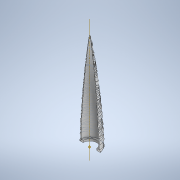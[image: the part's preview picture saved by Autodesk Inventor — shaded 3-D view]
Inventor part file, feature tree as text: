
AUTODESK INVENTOR PART (.ipt)
format: ipt  version: 2022 (Build 260153000, 153)  size: 3,374,080 bytes
history: native  units: in
note: dims shown in document units (in); Inventor stores cm internally (conversion verified against a paired STEP export)
features: sketch x9, helix x6, other x4, revolve x2, fillet x2, extrude x1
ambient origin geometry x8: Origin, YZ Plane, XZ Plane, XY Plane, X Axis, Y Axis, Z Axis, Center Point
bodies: Solid1 (feature_tree)
feature tree (24):
  other  "CrossSection1"
  other  "CrossSection2"
  extrude  "Extrusion1"  Depth=0.1969in
  revolve  "Revolution1"  Angle=360.0deg
  other  "Work Axis3"
  helix  "Coil3"  [1 undecoded]
  revolve  "Revolution2"  [1 undecoded]
  fillet  "Fillet2"  Radius=0.7677in
  other  "Work Axis7"
  helix  "Coil2"  [1 undecoded]
  fillet  "Fillet4"  Radius=0.1969in
  helix  "Coil4"  [1 undecoded]
  helix  "Coil5"  [1 undecoded]
  helix  "Coil6"  [1 undecoded]
  helix  "Coil7"  [1 undecoded]
  sketch  "Sketch1"  dims[d0=1.1811in d1=0.1969in]
  sketch  "Sketch2"  dims[d2=0.1181in d3=0.0in d7=360.0deg d8=0.4331in]
  sketch  "Sketch3"  dims[d19=0.4724in d20=0.2362in d21=0.7677in d22=360.0deg d24=0.1969in d26=0.1969in]
  sketch  "Sketch4"  dims[d29=1.5748in d30=0.3937in d31=1.378in d32=0.0447in d33=90.0deg d34=90.0deg d35=0.0in d36=0.0in d42=0.0787in d44=43.5197in d45=43.5039in]
  sketch  "Sketch5"  dims[d50=0.0in]
  sketch  "Sketch6"  dims[d54=0.3937in d55=0.3937in d56=5.5118in d57=-0.0275in d58=90.0deg d59=90.0deg d60=0.0in d61=0.0in]
  sketch  "Sketch7"  dims[d62=0.3937in]
  sketch  "Sketch8"  dims[d63=0.7677in]
  sketch  "Sketch9"  dims[d64=0.2362in d65=0.1575in d66=5.7087in d68=0.0394in d69=5.5118in d70=0.053in d71=0.0344in d72=0.0305in d73=0.1969in d74=0.2362in d75=0.1969in d77=0.0197in d78=0.0197in d79=0.2362in d80=0.2362in d81=0.2362in d82=0.2362in d83=0.1969in d84=0.0394in d86=0.0394in d87=0.2756in d88=0.2756in d89=0.2362in d90=0.7874in d91=0.3937in d92=3.937in d93=0.0412in d94=90.0deg d95=90.0deg d96=0.0in d97=0.0in d98=0.1181in d99=0.1181in d100=0.1181in d101=0.1575in d102=0.1575in d103=0.0236in d104=0.0236in d105=0.061in d107=0.7874in d108=0.3937in d109=3.937in d110=0.0481in d111=90.0deg d112=90.0deg d113=0.0in d114=0.0in d115=0.0197in d116=0.0787in d117=0.0in d118=0.7874in d119=0.3937in d120=0.1575in d121=0.1575in d122=0.1575in d123=0.6496in d124=0.2362in d125=0.2362in d127=0.0098in d128=0.0098in d129=1.1811in d130=0.3937in d131=1.9685in d132=-0.0206in d133=90.0deg d134=90.0deg d135=0.0in d136=0.0in d138=0.0787in d139=0.0315in d140=0.0315in d141=0.0315in d143=0.0433in d144=0.0394in d145=0.0067in d146=0.0394in d147=0.0067in d148=0.4724in d149=0.3937in d150=7.874in d151=0.055in d152=90.0deg d153=90.0deg d154=0.0in d155=0.0in d156=0.0157in d157=0.0197in d158=0.0787in d159=0.0in d160=0.7874in]
note: 7 required parameter values undecoded (feature->parameter linkage not recoverable at this tier; creation-order binding heuristic only, values carry confidence <= 0.55)